# Revit family: LF Northport Path Light
name_source: partatom
category: Lighting Fixtures
units: mm (PartAtom-declared; Revit-internal decimal feet)

## family parameters
Always vertical = Yes
Cut with Voids When Loaded = No
Light Source = Yes
OmniClass Number = 23.80.70.14.21
OmniClass Title = Street and Roadway Lighting
Part Type = Normal
Room Calculation Point = No
Round Connector Dimension = Use Diameter
Shared = No
Work Plane-Based = No

## types (1)
- 37"H
    Apparent Load = 100 VA
    Assembly Code = D5020200
    Color Filter = 16777215
    D = 0' - 8 1/2"
    Default Elevation = 0' - 0"
    Description = Path Light - DR400
    Diffuser Lens = LANDSCAPE FORMS - DIFFUSER - ILLUMINATED - LED
    Dimming Lamp Color Temperature Shift = <None>
    Emit Shape Visible in Rendering = No
    Emit from Circle Diameter = 1' - 0"
    H = 3' - 1"
    Lamp = Nichia 219C LED FR4 Circuit Board
    Load Classification = Lighting - Exterior
    Manufacturer = Landscape Forms
    Model = NORTHPORT
    Number of Poles = 1
    Photometric Web File = DR500-SO-T5.ies
    Tilt Angle = 90.00°
    URL = https://www.landscapeforms.com
    Voltage = 120 V
    W = 0' - 8 1/2"
    Wattage Comments = 20

## geometry (parser evidence)
native form markers: Sweep x1
no freeform markers — native parametric forms only
